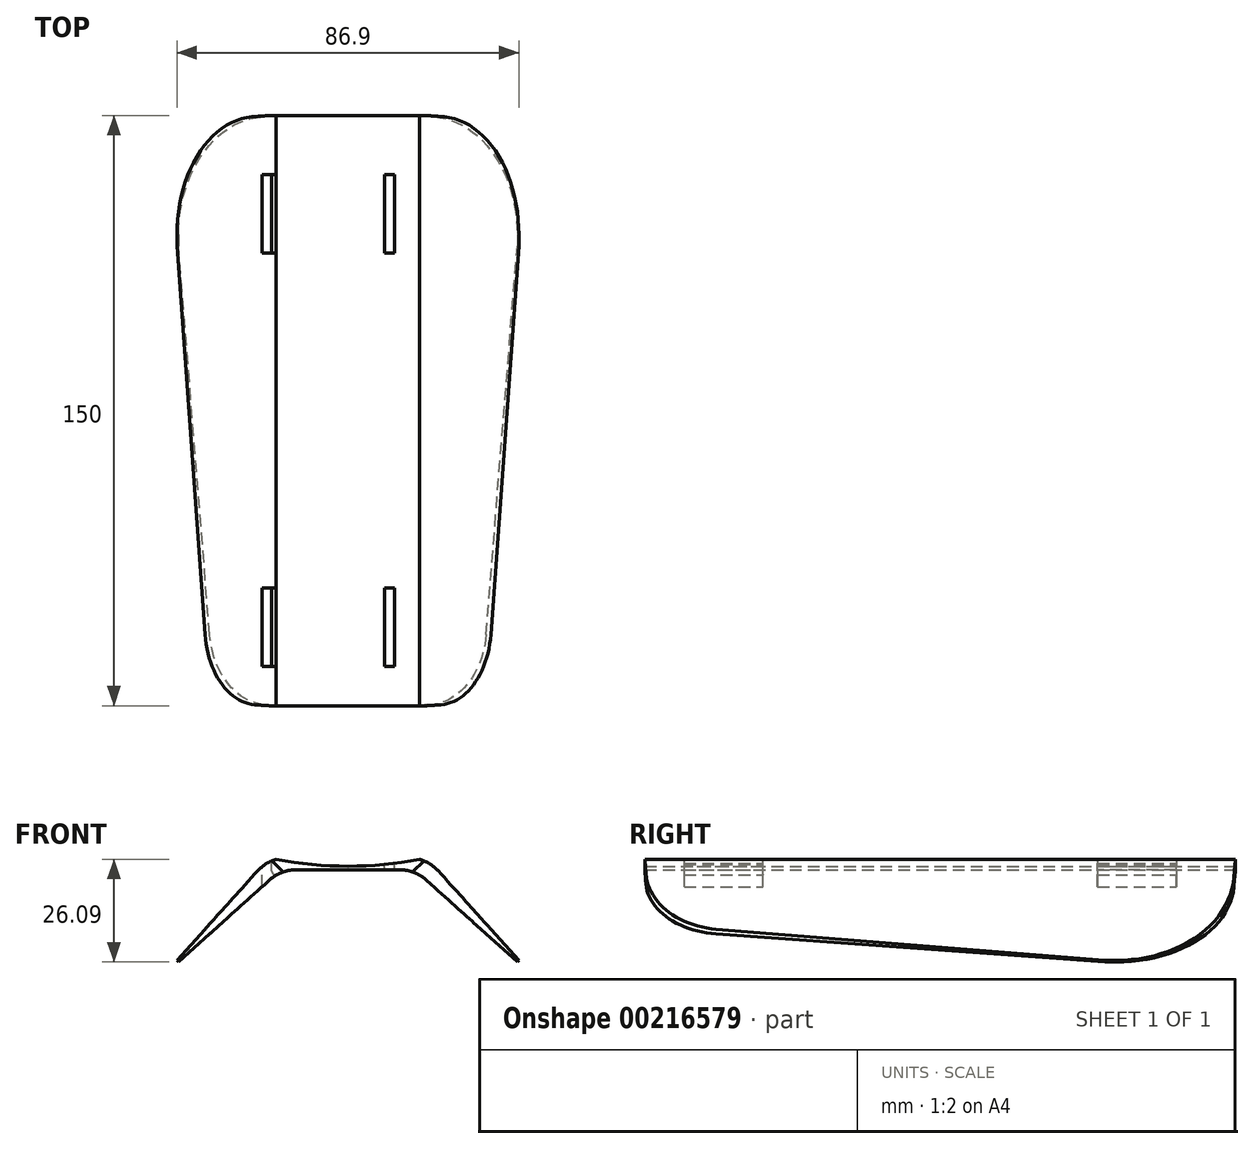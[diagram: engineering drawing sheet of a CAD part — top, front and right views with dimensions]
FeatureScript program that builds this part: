
annotation { "Feature Type Name" : "Feature", "Feature Type Description" : "" }
export const myFeature = defineFeature(function(context is Context, id is Id, definition is map)
    precondition{}
    {
        {
            var Q0;
            Q0=qCreatedBy(makeId("Top.planeOp"),FACE);
            var sketch = newSketch(context, id + "F0", { "sketchPlane" : qUnion([Q0])});
            skLineSegment(sketch, "E0.bottom", {"start": v(0, 150) * mm, "end": v(40, 150) * mm});
            skLineSegment(sketch, "E0.top", {"start": v(0, 0) * mm, "end": v(40, 0) * mm});
            skLineSegment(sketch, "E0.left", {"start": v(0, 150) * mm, "end": v(0, 0) * mm});
            skLineSegment(sketch, "E0.right", {"start": v(40, 150) * mm, "end": v(40, 0) * mm});
            skSolve(sketch);
        }
        {
            var Q0;
            Q0=makeQuery(id+"F0.imprint","IMPRINT",FACE,{"disambiguationData":[TD([[makeQuery(id+"F0.imprint","IMPRINT",EDGE,{"derivedFrom":sQuery(id+"F0.wireOp",EDGE,"E0.bottom")}),-1.0]])]});
            extrude(context, id + "F1", {"entities" : qUnion([Q0]), "depth" : 3 * mm});
        }
        {
            var Q0;
            Q0=makeQuery(id+"F1.opExtrude","SWEPT_FACE",FACE,{"disambiguationData":[OSD([sQuery(id+"F0.wireOp",EDGE,"E0.bottom")])]});
            var sketch = newSketch(context, id + "F2", { "sketchPlane" : qUnion([Q0])});
            skArc(sketch, "E1", {"start": v(-40, 3) * mm, "mid": v(-20, 0.9) * mm, "end": v(0, 3) * mm});
            skSolve(sketch);
        }
        {
            var Q0;
            Q0=makeQuery(id+"F1.opExtrude","CAP_EDGE",EDGE,{"disambiguationData":[OSD([sQuery(id+"F0.wireOp",EDGE,"E0.left")])],"isStart":true});
            var Q1;
            Q1=makeQuery(id+"F1.opExtrude","CAP_EDGE",EDGE,{"disambiguationData":[OSD([sQuery(id+"F0.wireOp",EDGE,"E0.right")])],"isStart":true});
            chamfer(context, id + "F3", {"entities" : qUnion([Q0, Q1]), "chamferType" : ChamferType.OFFSET_ANGLE, "width" : 3 * mm, "oppositeDirection" : false, "angle" : 45 * degree, "tangentPropagation" : true});
        }
        {
            var Q0;
            Q0=makeQuery(id+"F3.opChamfer","BLEND_FACE",FACE,{"disambiguationData":[OSD([sQuery(id+"F0.wireOp",EDGE,"E0.right")])]});
            extrude(context, id + "F4", {"entities" : qUnion([Q0]), "operationType" : NewBodyOperationType.ADD, "depth" : 35 * mm, "hasDraft" : true, "draftAngle" : 3 * degree, "draftPullDirection" : true});
        }
        {
            var Q0;
            Q0=makeQuery(id+"F3.opChamfer","BLEND_FACE",FACE,{"disambiguationData":[OSD([sQuery(id+"F0.wireOp",EDGE,"E0.left")])]});
            extrude(context, id + "F5", {"entities" : qUnion([Q0]), "operationType" : NewBodyOperationType.ADD, "depth" : 35 * mm, "hasDraft" : true, "draftAngle" : 3 * degree, "draftPullDirection" : true});
        }
        {
            var Q0;
            {var subQ0=sQuery(id+"F0.wireOp",EDGE,"E0.right");var subQ1=sQuery(id+"F0.wireOp",EDGE,"E0.left");var subQ2=sQuery(id+"F0.wireOp",EDGE,"E0.top");var subQ3=sQuery(id+"F0.wireOp",EDGE,"E0.bottom");var subQ4=makeQuery(id+"F3.opChamfer","BLEND_EDGE",EDGE,{"blendedFrom":[makeQuery(id+"F1.opExtrude","CAP_EDGE",EDGE,{"disambiguationData":[OSD([subQ0])],"isStart":true}),makeQuery(id+"F1.opExtrude","CAP_FACE",FACE,{"disambiguationData":[OSD([subQ3,subQ2,subQ1,subQ0])],"isStart":false})],"blendedInto":[makeQuery(id+"F1.opExtrude","CAP_FACE",FACE,{"disambiguationData":[OSD([subQ3,subQ2,subQ1,subQ0])],"isStart":false})]});Q0=makeQuery(id+"F4.boolean.opBoolean","MERGE",EDGE,{"derivedFrom":[subQ4,makeQuery(id+"F4.opExtrude","CAP_EDGE",EDGE,{"disambiguationData":[OSD([subQ3,subQ2,subQ1,subQ0]),TDD([subQ4])],"isStart":true})]});}
            var Q1;
            {var subQ0=sQuery(id+"F0.wireOp",EDGE,"E0.right");var subQ1=sQuery(id+"F0.wireOp",EDGE,"E0.left");var subQ2=sQuery(id+"F0.wireOp",EDGE,"E0.top");var subQ3=sQuery(id+"F0.wireOp",EDGE,"E0.bottom");var subQ4=makeQuery(id+"F3.opChamfer","BLEND_EDGE",EDGE,{"blendedFrom":[makeQuery(id+"F1.opExtrude","CAP_EDGE",EDGE,{"disambiguationData":[OSD([subQ1])],"isStart":true}),makeQuery(id+"F1.opExtrude","CAP_FACE",FACE,{"disambiguationData":[OSD([subQ3,subQ2,subQ1,subQ0])],"isStart":false})],"blendedInto":[makeQuery(id+"F1.opExtrude","CAP_FACE",FACE,{"disambiguationData":[OSD([subQ3,subQ2,subQ1,subQ0])],"isStart":false})]});Q1=makeQuery(id+"F5.boolean.opBoolean","MERGE",EDGE,{"derivedFrom":[subQ4,makeQuery(id+"F5.opExtrude","CAP_EDGE",EDGE,{"disambiguationData":[OSD([subQ3,subQ2,subQ1,subQ0]),TDD([subQ4])],"isStart":true})]});}
            var Q2;
            {var subQ0=sQuery(id+"F0.wireOp",EDGE,"E0.right");var subQ1=sQuery(id+"F0.wireOp",EDGE,"E0.left");var subQ2=sQuery(id+"F0.wireOp",EDGE,"E0.top");var subQ3=sQuery(id+"F0.wireOp",EDGE,"E0.bottom");var subQ4=makeQuery(id+"F3.opChamfer","BLEND_EDGE",EDGE,{"blendedFrom":[makeQuery(id+"F1.opExtrude","CAP_EDGE",EDGE,{"disambiguationData":[OSD([subQ0])],"isStart":true}),makeQuery(id+"F1.opExtrude","CAP_FACE",FACE,{"disambiguationData":[OSD([subQ3,subQ2,subQ1,subQ0])],"isStart":true})],"blendedInto":[makeQuery(id+"F1.opExtrude","CAP_FACE",FACE,{"disambiguationData":[OSD([subQ3,subQ2,subQ1,subQ0])],"isStart":true})]});Q2=makeQuery(id+"F4.boolean.opBoolean","MERGE",EDGE,{"derivedFrom":[subQ4,makeQuery(id+"F4.opExtrude","CAP_EDGE",EDGE,{"disambiguationData":[OSD([subQ3,subQ2,subQ1,subQ0]),TDD([subQ4])],"isStart":true})]});}
            var Q3;
            {var subQ0=sQuery(id+"F0.wireOp",EDGE,"E0.right");var subQ1=sQuery(id+"F0.wireOp",EDGE,"E0.left");var subQ2=sQuery(id+"F0.wireOp",EDGE,"E0.top");var subQ3=sQuery(id+"F0.wireOp",EDGE,"E0.bottom");var subQ4=makeQuery(id+"F3.opChamfer","BLEND_EDGE",EDGE,{"blendedFrom":[makeQuery(id+"F1.opExtrude","CAP_EDGE",EDGE,{"disambiguationData":[OSD([subQ1])],"isStart":true}),makeQuery(id+"F1.opExtrude","CAP_FACE",FACE,{"disambiguationData":[OSD([subQ3,subQ2,subQ1,subQ0])],"isStart":true})],"blendedInto":[makeQuery(id+"F1.opExtrude","CAP_FACE",FACE,{"disambiguationData":[OSD([subQ3,subQ2,subQ1,subQ0])],"isStart":true})]});Q3=makeQuery(id+"F5.boolean.opBoolean","MERGE",EDGE,{"derivedFrom":[subQ4,makeQuery(id+"F5.opExtrude","CAP_EDGE",EDGE,{"disambiguationData":[OSD([subQ3,subQ2,subQ1,subQ0]),TDD([subQ4])],"isStart":true})]});}
            fillet(context, id + "F6", {"entities" : qUnion([Q0, Q1, Q2, Q3]), "radius" : 10 * mm, "tangentPropagation" : true, "allowEdgeOverflow" : false});
        }
        {
            var Q0;
            Q0=makeQuery(id+"F5.opExtrude","CAP_EDGE",EDGE,{"disambiguationData":[OSD([sQuery(id+"F0.wireOp",EDGE,"E0.bottom"),sQuery(id+"F0.wireOp",EDGE,"E0.left")])],"isStart":false});
            var Q1;
            Q1=makeQuery(id+"F4.opExtrude","CAP_EDGE",EDGE,{"disambiguationData":[OSD([sQuery(id+"F0.wireOp",EDGE,"E0.bottom"),sQuery(id+"F0.wireOp",EDGE,"E0.right")])],"isStart":false});
            fillet(context, id + "F7", {"entities" : qUnion([Q0, Q1]), "radius" : 30 * mm, "tangentPropagation" : true, "allowEdgeOverflow" : false});
        }
        {
            var Q0;
            Q0=makeQuery(id+"F5.opExtrude","CAP_EDGE",EDGE,{"disambiguationData":[OSD([sQuery(id+"F0.wireOp",EDGE,"E0.top"),sQuery(id+"F0.wireOp",EDGE,"E0.left")])],"isStart":false});
            var Q1;
            Q1=makeQuery(id+"F4.opExtrude","CAP_EDGE",EDGE,{"disambiguationData":[OSD([sQuery(id+"F0.wireOp",EDGE,"E0.top"),sQuery(id+"F0.wireOp",EDGE,"E0.right")])],"isStart":false});
            chamfer(context, id + "F8", {"entities" : qUnion([Q0, Q1]), "chamferType" : ChamferType.TWO_OFFSETS, "width1" : 12.5 * mm, "oppositeDirection" : false, "width2" : 115 * mm, "tangentPropagation" : true});
        }
        {
            var Q0;
            {var subQ0=sQuery(id+"F0.wireOp",EDGE,"E0.left");var subQ1=sQuery(id+"F0.wireOp",EDGE,"E0.top");Q0=makeQuery(id+"F8.opChamfer","BLEND_EDGE",EDGE,{"blendedFrom":[makeQuery(id+"F5.opExtrude","CAP_EDGE",EDGE,{"disambiguationData":[OSD([subQ1,subQ0])],"isStart":false}),makeQuery(id+"F5.opExtrude","SWEPT_FACE",FACE,{"disambiguationData":[OSD([subQ1,subQ0])]})],"blendedInto":[makeQuery(id+"F5.opExtrude","SWEPT_FACE",FACE,{"disambiguationData":[OSD([subQ1,subQ0])]})]});}
            var Q1;
            {var subQ0=sQuery(id+"F0.wireOp",EDGE,"E0.right");var subQ1=sQuery(id+"F0.wireOp",EDGE,"E0.top");Q1=makeQuery(id+"F8.opChamfer","BLEND_EDGE",EDGE,{"blendedFrom":[makeQuery(id+"F4.opExtrude","CAP_EDGE",EDGE,{"disambiguationData":[OSD([subQ1,subQ0])],"isStart":false}),makeQuery(id+"F4.opExtrude","SWEPT_FACE",FACE,{"disambiguationData":[OSD([subQ1,subQ0])]})],"blendedInto":[makeQuery(id+"F4.opExtrude","SWEPT_FACE",FACE,{"disambiguationData":[OSD([subQ1,subQ0])]})]});}
            fillet(context, id + "F9", {"entities" : qUnion([Q0, Q1]), "radius" : 20 * mm, "tangentPropagation" : true, "allowEdgeOverflow" : false});
        }
        {
            var Q0;
            Q0=makeQuery(id+"F2.imprint","IMPRINT",FACE,{"disambiguationData":[TD([[makeQuery(id+"F2.imprint","IMPRINT",EDGE,{"derivedFrom":sQuery(id+"F2.wireOp",EDGE,"E1")}),1.0]])]});
            extrude(context, id + "F10", {"entities" : qUnion([Q0]), "operationType" : NewBodyOperationType.REMOVE, "endBound" : BoundingType.UP_TO_NEXT, "oppositeDirection" : true, "depth" : 25 * mm});
        }
        {
            var Q0;
            Q0=qCreatedBy(makeId("Top.planeOp"),FACE);
            var sketch = newSketch(context, id + "F11", { "sketchPlane" : qUnion([Q0])});
            skLineSegment(sketch, "E2.bottom", {"start": v(29.34, 10) * mm, "end": v(31.84, 10) * mm});
            skLineSegment(sketch, "E2.top", {"start": v(29.34, 30) * mm, "end": v(31.84, 30) * mm});
            skLineSegment(sketch, "E2.left", {"start": v(29.34, 10) * mm, "end": v(29.34, 30) * mm});
            skLineSegment(sketch, "E2.right", {"start": v(31.84, 10) * mm, "end": v(31.84, 30) * mm});
            skLineSegment(sketch, "E3.bottom", {"start": v(0.65, 30) * mm, "end": v(-1.85, 30) * mm});
            skLineSegment(sketch, "E3.top", {"start": v(0.65, 10) * mm, "end": v(-1.85, 10) * mm});
            skLineSegment(sketch, "E3.left", {"start": v(0.65, 30) * mm, "end": v(0.65, 10) * mm});
            skLineSegment(sketch, "E3.right", {"start": v(-1.85, 30) * mm, "end": v(-1.85, 10) * mm});
            skLineSegment(sketch, "E4.bottom", {"start": v(-1.85, 135) * mm, "end": v(0.65, 135) * mm});
            skLineSegment(sketch, "E4.top", {"start": v(-1.85, 115) * mm, "end": v(0.65, 115) * mm});
            skLineSegment(sketch, "E4.left", {"start": v(-1.85, 135) * mm, "end": v(-1.85, 115) * mm});
            skLineSegment(sketch, "E4.right", {"start": v(0.65, 135) * mm, "end": v(0.65, 115) * mm});
            skLineSegment(sketch, "E5.bottom", {"start": v(29.34, 135) * mm, "end": v(31.84, 135) * mm});
            skLineSegment(sketch, "E5.top", {"start": v(29.34, 115) * mm, "end": v(31.84, 115) * mm});
            skLineSegment(sketch, "E5.left", {"start": v(29.34, 135) * mm, "end": v(29.34, 115) * mm});
            skLineSegment(sketch, "E5.right", {"start": v(31.84, 135) * mm, "end": v(31.84, 115) * mm});
            skSolve(sketch);
        }
        {
            var Q0;
            Q0=makeQuery(id+"F11.imprint","IMPRINT",FACE,{"disambiguationData":[TD([[makeQuery(id+"F11.imprint","IMPRINT",EDGE,{"derivedFrom":sQuery(id+"F11.wireOp",EDGE,"E4.bottom")}),-1.0]])]});
            var Q1;
            Q1=makeQuery(id+"F11.imprint","IMPRINT",FACE,{"disambiguationData":[TD([[makeQuery(id+"F11.imprint","IMPRINT",EDGE,{"derivedFrom":sQuery(id+"F11.wireOp",EDGE,"E5.bottom")}),-1.0]])]});
            var Q2;
            Q2=makeQuery(id+"F11.imprint","IMPRINT",FACE,{"disambiguationData":[TD([[makeQuery(id+"F11.imprint","IMPRINT",EDGE,{"derivedFrom":sQuery(id+"F11.wireOp",EDGE,"E2.bottom")}),1.0]])]});
            var Q3;
            Q3=makeQuery(id+"F11.imprint","IMPRINT",FACE,{"disambiguationData":[TD([[makeQuery(id+"F11.imprint","IMPRINT",EDGE,{"derivedFrom":sQuery(id+"F11.wireOp",EDGE,"E3.bottom")}),1.0]])]});
            extrude(context, id + "F12", {"entities" : qUnion([Q0, Q1, Q2, Q3]), "operationType" : NewBodyOperationType.REMOVE, "endBound" : BoundingType.SYMMETRIC, "oppositeDirection" : true, "depth" : 10 * mm});
        }
        {
            var Q0;
            {var subQ0=sQuery(id+"F0.wireOp",EDGE,"E0.right");var subQ1=sQuery(id+"F0.wireOp",EDGE,"E0.left");var subQ2=sQuery(id+"F0.wireOp",EDGE,"E0.top");var subQ3=sQuery(id+"F0.wireOp",EDGE,"E0.bottom");var subQ4=makeQuery(id+"F3.opChamfer","BLEND_EDGE",EDGE,{"blendedFrom":[makeQuery(id+"F1.opExtrude","CAP_EDGE",EDGE,{"disambiguationData":[OSD([subQ1])],"isStart":true}),makeQuery(id+"F1.opExtrude","CAP_FACE",FACE,{"disambiguationData":[OSD([subQ3,subQ2,subQ1,subQ0])],"isStart":true})],"blendedInto":[makeQuery(id+"F1.opExtrude","CAP_FACE",FACE,{"disambiguationData":[OSD([subQ3,subQ2,subQ1,subQ0])],"isStart":true})]});Q0=makeQuery(id+"F12.boolean.opBoolean","INTERSECT",EDGE,{"derivedFrom":[makeQuery(id+"F6.opFillet","BLEND_FACE",FACE,{"disambiguationData":[OSD([subQ3,subQ2,subQ1,subQ0]),TDD([makeQuery(id+"F5.boolean.opBoolean","MERGE",EDGE,{"derivedFrom":[subQ4,makeQuery(id+"F5.opExtrude","CAP_EDGE",EDGE,{"disambiguationData":[OSD([subQ3,subQ2,subQ1,subQ0]),TDD([subQ4])],"isStart":true})]})])]}),makeQuery(id+"F12.opExtrude","SWEPT_FACE",FACE,{"disambiguationData":[OSD([sQuery(id+"F11.wireOp",EDGE,"E4.right")])]})]});}
            var Q1;
            {var subQ0=sQuery(id+"F0.wireOp",EDGE,"E0.right");var subQ1=sQuery(id+"F0.wireOp",EDGE,"E0.left");var subQ2=sQuery(id+"F0.wireOp",EDGE,"E0.top");var subQ3=sQuery(id+"F0.wireOp",EDGE,"E0.bottom");var subQ4=makeQuery(id+"F3.opChamfer","BLEND_EDGE",EDGE,{"blendedFrom":[makeQuery(id+"F1.opExtrude","CAP_EDGE",EDGE,{"disambiguationData":[OSD([subQ0])],"isStart":true}),makeQuery(id+"F1.opExtrude","CAP_FACE",FACE,{"disambiguationData":[OSD([subQ3,subQ2,subQ1,subQ0])],"isStart":true})],"blendedInto":[makeQuery(id+"F1.opExtrude","CAP_FACE",FACE,{"disambiguationData":[OSD([subQ3,subQ2,subQ1,subQ0])],"isStart":true})]});Q1=makeQuery(id+"F12.boolean.opBoolean","INTERSECT",EDGE,{"derivedFrom":[makeQuery(id+"F6.opFillet","BLEND_FACE",FACE,{"disambiguationData":[OSD([subQ3,subQ2,subQ1,subQ0]),TDD([makeQuery(id+"F4.boolean.opBoolean","MERGE",EDGE,{"derivedFrom":[subQ4,makeQuery(id+"F4.opExtrude","CAP_EDGE",EDGE,{"disambiguationData":[OSD([subQ3,subQ2,subQ1,subQ0]),TDD([subQ4])],"isStart":true})]})])]}),makeQuery(id+"F12.opExtrude","SWEPT_FACE",FACE,{"disambiguationData":[OSD([sQuery(id+"F11.wireOp",EDGE,"E5.left")])]})]});}
            var Q2;
            {var subQ0=sQuery(id+"F0.wireOp",EDGE,"E0.right");var subQ1=sQuery(id+"F0.wireOp",EDGE,"E0.left");var subQ2=sQuery(id+"F0.wireOp",EDGE,"E0.top");var subQ3=sQuery(id+"F0.wireOp",EDGE,"E0.bottom");var subQ4=makeQuery(id+"F3.opChamfer","BLEND_EDGE",EDGE,{"blendedFrom":[makeQuery(id+"F1.opExtrude","CAP_EDGE",EDGE,{"disambiguationData":[OSD([subQ0])],"isStart":true}),makeQuery(id+"F1.opExtrude","CAP_FACE",FACE,{"disambiguationData":[OSD([subQ3,subQ2,subQ1,subQ0])],"isStart":true})],"blendedInto":[makeQuery(id+"F1.opExtrude","CAP_FACE",FACE,{"disambiguationData":[OSD([subQ3,subQ2,subQ1,subQ0])],"isStart":true})]});Q2=makeQuery(id+"F12.boolean.opBoolean","INTERSECT",EDGE,{"derivedFrom":[makeQuery(id+"F6.opFillet","BLEND_FACE",FACE,{"disambiguationData":[OSD([subQ3,subQ2,subQ1,subQ0]),TDD([makeQuery(id+"F4.boolean.opBoolean","MERGE",EDGE,{"derivedFrom":[subQ4,makeQuery(id+"F4.opExtrude","CAP_EDGE",EDGE,{"disambiguationData":[OSD([subQ3,subQ2,subQ1,subQ0]),TDD([subQ4])],"isStart":true})]})])]}),makeQuery(id+"F12.opExtrude","SWEPT_FACE",FACE,{"disambiguationData":[OSD([sQuery(id+"F11.wireOp",EDGE,"E2.left")])]})]});}
            var Q3;
            {var subQ0=sQuery(id+"F0.wireOp",EDGE,"E0.right");var subQ1=sQuery(id+"F0.wireOp",EDGE,"E0.left");var subQ2=sQuery(id+"F0.wireOp",EDGE,"E0.top");var subQ3=sQuery(id+"F0.wireOp",EDGE,"E0.bottom");var subQ4=makeQuery(id+"F3.opChamfer","BLEND_EDGE",EDGE,{"blendedFrom":[makeQuery(id+"F1.opExtrude","CAP_EDGE",EDGE,{"disambiguationData":[OSD([subQ1])],"isStart":true}),makeQuery(id+"F1.opExtrude","CAP_FACE",FACE,{"disambiguationData":[OSD([subQ3,subQ2,subQ1,subQ0])],"isStart":true})],"blendedInto":[makeQuery(id+"F1.opExtrude","CAP_FACE",FACE,{"disambiguationData":[OSD([subQ3,subQ2,subQ1,subQ0])],"isStart":true})]});Q3=makeQuery(id+"F12.boolean.opBoolean","INTERSECT",EDGE,{"derivedFrom":[makeQuery(id+"F6.opFillet","BLEND_FACE",FACE,{"disambiguationData":[OSD([subQ3,subQ2,subQ1,subQ0]),TDD([makeQuery(id+"F5.boolean.opBoolean","MERGE",EDGE,{"derivedFrom":[subQ4,makeQuery(id+"F5.opExtrude","CAP_EDGE",EDGE,{"disambiguationData":[OSD([subQ3,subQ2,subQ1,subQ0]),TDD([subQ4])],"isStart":true})]})])]}),makeQuery(id+"F12.opExtrude","SWEPT_FACE",FACE,{"disambiguationData":[OSD([sQuery(id+"F11.wireOp",EDGE,"E3.left")])]})]});}
            var Q4;
            {var subQ0=sQuery(id+"F0.wireOp",EDGE,"E0.right");var subQ1=sQuery(id+"F0.wireOp",EDGE,"E0.left");var subQ2=sQuery(id+"F0.wireOp",EDGE,"E0.top");var subQ3=sQuery(id+"F0.wireOp",EDGE,"E0.bottom");var subQ4=makeQuery(id+"F3.opChamfer","BLEND_EDGE",EDGE,{"blendedFrom":[makeQuery(id+"F1.opExtrude","CAP_EDGE",EDGE,{"disambiguationData":[OSD([subQ0])],"isStart":true}),makeQuery(id+"F1.opExtrude","CAP_FACE",FACE,{"disambiguationData":[OSD([subQ3,subQ2,subQ1,subQ0])],"isStart":false})],"blendedInto":[makeQuery(id+"F1.opExtrude","CAP_FACE",FACE,{"disambiguationData":[OSD([subQ3,subQ2,subQ1,subQ0])],"isStart":false})]});Q4=makeQuery(id+"F12.boolean.opBoolean","INTERSECT",EDGE,{"derivedFrom":[makeQuery(id+"F6.opFillet","BLEND_FACE",FACE,{"disambiguationData":[OSD([subQ3,subQ2,subQ1,subQ0]),TDD([makeQuery(id+"F4.boolean.opBoolean","MERGE",EDGE,{"derivedFrom":[subQ4,makeQuery(id+"F4.opExtrude","CAP_EDGE",EDGE,{"disambiguationData":[OSD([subQ3,subQ2,subQ1,subQ0]),TDD([subQ4])],"isStart":true})]})])]}),makeQuery(id+"F12.opExtrude","SWEPT_FACE",FACE,{"disambiguationData":[OSD([sQuery(id+"F11.wireOp",EDGE,"E2.left")])]})]});}
            var Q5;
            {var subQ0=sQuery(id+"F0.wireOp",EDGE,"E0.right");var subQ1=sQuery(id+"F0.wireOp",EDGE,"E0.left");var subQ2=sQuery(id+"F0.wireOp",EDGE,"E0.top");var subQ3=sQuery(id+"F0.wireOp",EDGE,"E0.bottom");var subQ4=makeQuery(id+"F3.opChamfer","BLEND_EDGE",EDGE,{"blendedFrom":[makeQuery(id+"F1.opExtrude","CAP_EDGE",EDGE,{"disambiguationData":[OSD([subQ1])],"isStart":true}),makeQuery(id+"F1.opExtrude","CAP_FACE",FACE,{"disambiguationData":[OSD([subQ3,subQ2,subQ1,subQ0])],"isStart":false})],"blendedInto":[makeQuery(id+"F1.opExtrude","CAP_FACE",FACE,{"disambiguationData":[OSD([subQ3,subQ2,subQ1,subQ0])],"isStart":false})]});Q5=makeQuery(id+"F12.boolean.opBoolean","INTERSECT",EDGE,{"derivedFrom":[makeQuery(id+"F6.opFillet","BLEND_FACE",FACE,{"disambiguationData":[OSD([subQ3,subQ2,subQ1,subQ0]),TDD([makeQuery(id+"F5.boolean.opBoolean","MERGE",EDGE,{"derivedFrom":[subQ4,makeQuery(id+"F5.opExtrude","CAP_EDGE",EDGE,{"disambiguationData":[OSD([subQ3,subQ2,subQ1,subQ0]),TDD([subQ4])],"isStart":true})]})])]}),makeQuery(id+"F12.opExtrude","SWEPT_FACE",FACE,{"disambiguationData":[OSD([sQuery(id+"F11.wireOp",EDGE,"E3.left")])]})]});}
            var Q6;
            {var subQ0=sQuery(id+"F0.wireOp",EDGE,"E0.right");var subQ1=sQuery(id+"F0.wireOp",EDGE,"E0.left");var subQ2=sQuery(id+"F0.wireOp",EDGE,"E0.top");var subQ3=sQuery(id+"F0.wireOp",EDGE,"E0.bottom");var subQ4=makeQuery(id+"F3.opChamfer","BLEND_EDGE",EDGE,{"blendedFrom":[makeQuery(id+"F1.opExtrude","CAP_EDGE",EDGE,{"disambiguationData":[OSD([subQ1])],"isStart":true}),makeQuery(id+"F1.opExtrude","CAP_FACE",FACE,{"disambiguationData":[OSD([subQ3,subQ2,subQ1,subQ0])],"isStart":false})],"blendedInto":[makeQuery(id+"F1.opExtrude","CAP_FACE",FACE,{"disambiguationData":[OSD([subQ3,subQ2,subQ1,subQ0])],"isStart":false})]});Q6=makeQuery(id+"F12.boolean.opBoolean","INTERSECT",EDGE,{"derivedFrom":[makeQuery(id+"F6.opFillet","BLEND_FACE",FACE,{"disambiguationData":[OSD([subQ3,subQ2,subQ1,subQ0]),TDD([makeQuery(id+"F5.boolean.opBoolean","MERGE",EDGE,{"derivedFrom":[subQ4,makeQuery(id+"F5.opExtrude","CAP_EDGE",EDGE,{"disambiguationData":[OSD([subQ3,subQ2,subQ1,subQ0]),TDD([subQ4])],"isStart":true})]})])]}),makeQuery(id+"F12.opExtrude","SWEPT_FACE",FACE,{"disambiguationData":[OSD([sQuery(id+"F11.wireOp",EDGE,"E4.right")])]})]});}
            var Q7;
            {var subQ0=sQuery(id+"F0.wireOp",EDGE,"E0.right");var subQ1=sQuery(id+"F0.wireOp",EDGE,"E0.left");var subQ2=sQuery(id+"F0.wireOp",EDGE,"E0.top");var subQ3=sQuery(id+"F0.wireOp",EDGE,"E0.bottom");var subQ4=makeQuery(id+"F3.opChamfer","BLEND_EDGE",EDGE,{"blendedFrom":[makeQuery(id+"F1.opExtrude","CAP_EDGE",EDGE,{"disambiguationData":[OSD([subQ0])],"isStart":true}),makeQuery(id+"F1.opExtrude","CAP_FACE",FACE,{"disambiguationData":[OSD([subQ3,subQ2,subQ1,subQ0])],"isStart":false})],"blendedInto":[makeQuery(id+"F1.opExtrude","CAP_FACE",FACE,{"disambiguationData":[OSD([subQ3,subQ2,subQ1,subQ0])],"isStart":false})]});Q7=makeQuery(id+"F12.boolean.opBoolean","INTERSECT",EDGE,{"derivedFrom":[makeQuery(id+"F6.opFillet","BLEND_FACE",FACE,{"disambiguationData":[OSD([subQ3,subQ2,subQ1,subQ0]),TDD([makeQuery(id+"F4.boolean.opBoolean","MERGE",EDGE,{"derivedFrom":[subQ4,makeQuery(id+"F4.opExtrude","CAP_EDGE",EDGE,{"disambiguationData":[OSD([subQ3,subQ2,subQ1,subQ0]),TDD([subQ4])],"isStart":true})]})])]}),makeQuery(id+"F12.opExtrude","SWEPT_FACE",FACE,{"disambiguationData":[OSD([sQuery(id+"F11.wireOp",EDGE,"E5.left")])]})]});}
            fillet(context, id + "F13", {"entities" : qUnion([Q0, Q1, Q2, Q3, Q4, Q5, Q6, Q7]), "radius" : 1 * mm, "tangentPropagation" : true, "allowEdgeOverflow" : false});
        }
    });
